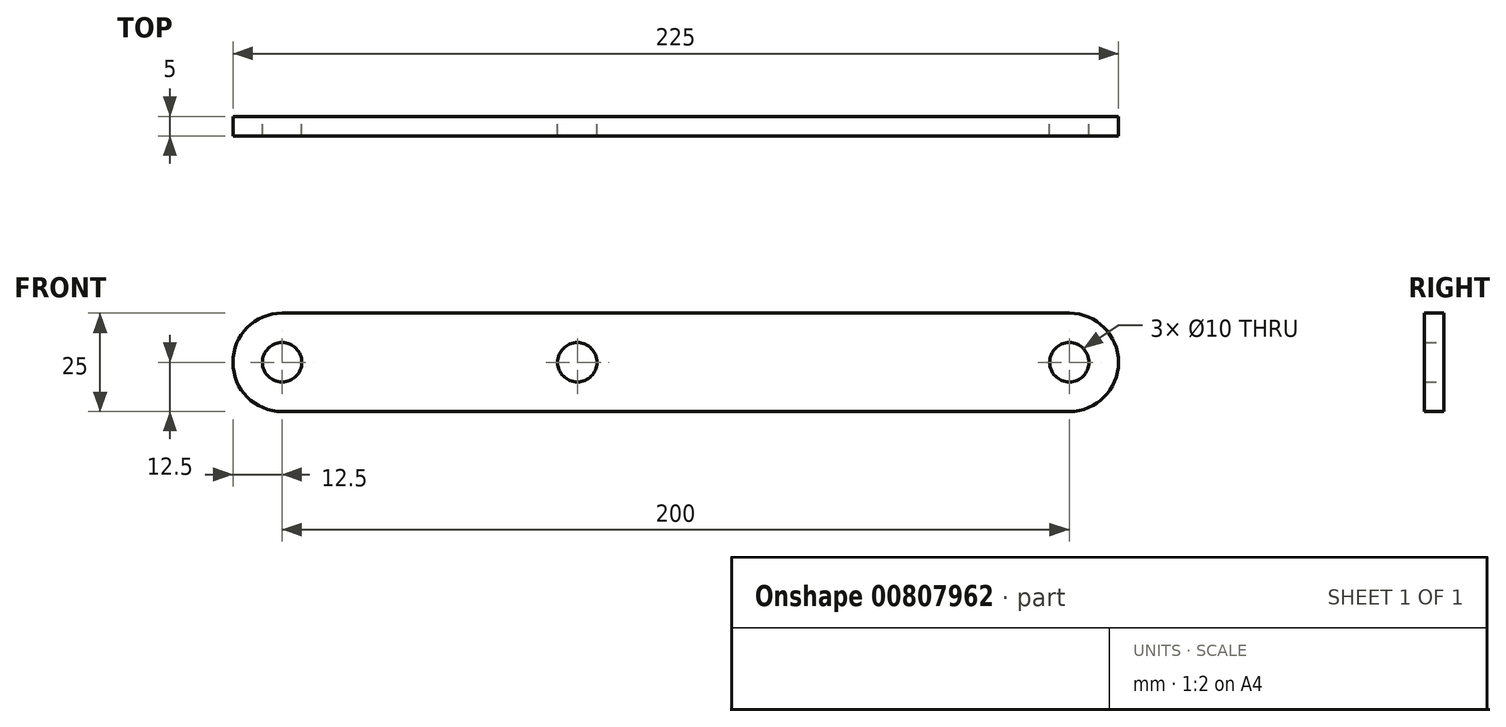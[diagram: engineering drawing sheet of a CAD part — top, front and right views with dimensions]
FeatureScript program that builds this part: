
annotation { "Feature Type Name" : "Feature", "Feature Type Description" : "" }
export const myFeature = defineFeature(function(context is Context, id is Id, definition is map)
    precondition{}
    {
        {
            var Q0;
            Q0=qCreatedBy(makeId("Front.planeOp"),FACE);
            var sketch = newSketch(context, id + "F0", { "sketchPlane" : qUnion([Q0])});
            skLineSegment(sketch, "E0.bottom", {"start": v(0, 0) * mm, "end": v(200, 0) * mm});
            skLineSegment(sketch, "E0.top", {"start": v(0, 25) * mm, "end": v(200, 25) * mm});
            skArc(sketch, "E1", {"start": v(0, 25) * mm, "mid": v(-12.5, 12.5) * mm, "end": v(0, 0) * mm});
            skArc(sketch, "E2", {"start": v(0, 17.5) * mm, "mid": v(-5, 12.5) * mm, "end": v(0, 7.5) * mm});
            skCircle(sketch, "E3", {"center": v(200, 12.5) * mm, "radius": 5 * mm});
            skArc(sketch, "E4", {"start": v(200, 0) * mm, "mid": v(212.5, 12.5) * mm, "end": v(200, 25) * mm});
            skArc(sketch, "E5", {"start": v(75, 7.5) * mm, "mid": v(80, 12.5) * mm, "end": v(75, 17.5) * mm});
            skLineSegment(sketch, "E6", {"start": v(0, 12.5) * mm, "end": v(-29.08, 12.5) * mm, "construction": true});
            skPoint(sketch, "E6.endSnap0", {"position": v(-12.5, 12.5) * mm});
            skLineSegment(sketch, "E7", {"start": v(-29.08, 12.5) * mm, "end": v(0, 12.5) * mm, "construction": true});
            skLineSegment(sketch, "E8", {"start": v(0, 12.5) * mm, "end": v(0, -17.12) * mm, "construction": true});
            skCircle(sketch, "E9", {"center": v(0, 12.5) * mm, "radius": 5 * mm});
            skCircle(sketch, "E10", {"center": v(75, 12.5) * mm, "radius": 5 * mm});
            skSolve(sketch);
        }
        {
            var Q0;
            Q0=makeQuery(id+"F0.imprint","IMPRINT",FACE,{"disambiguationData":[TD([[makeQuery(id+"F0.imprint","IMPRINT",EDGE,{"derivedFrom":sQuery(id+"F0.wireOp",EDGE,"E0.bottom")}),1.0]])]});
            extrude(context, id + "F1", {"entities" : qUnion([Q0]), "depth" : 5 * mm, "offsetDistance" : 25 * mm});
        }
    });
